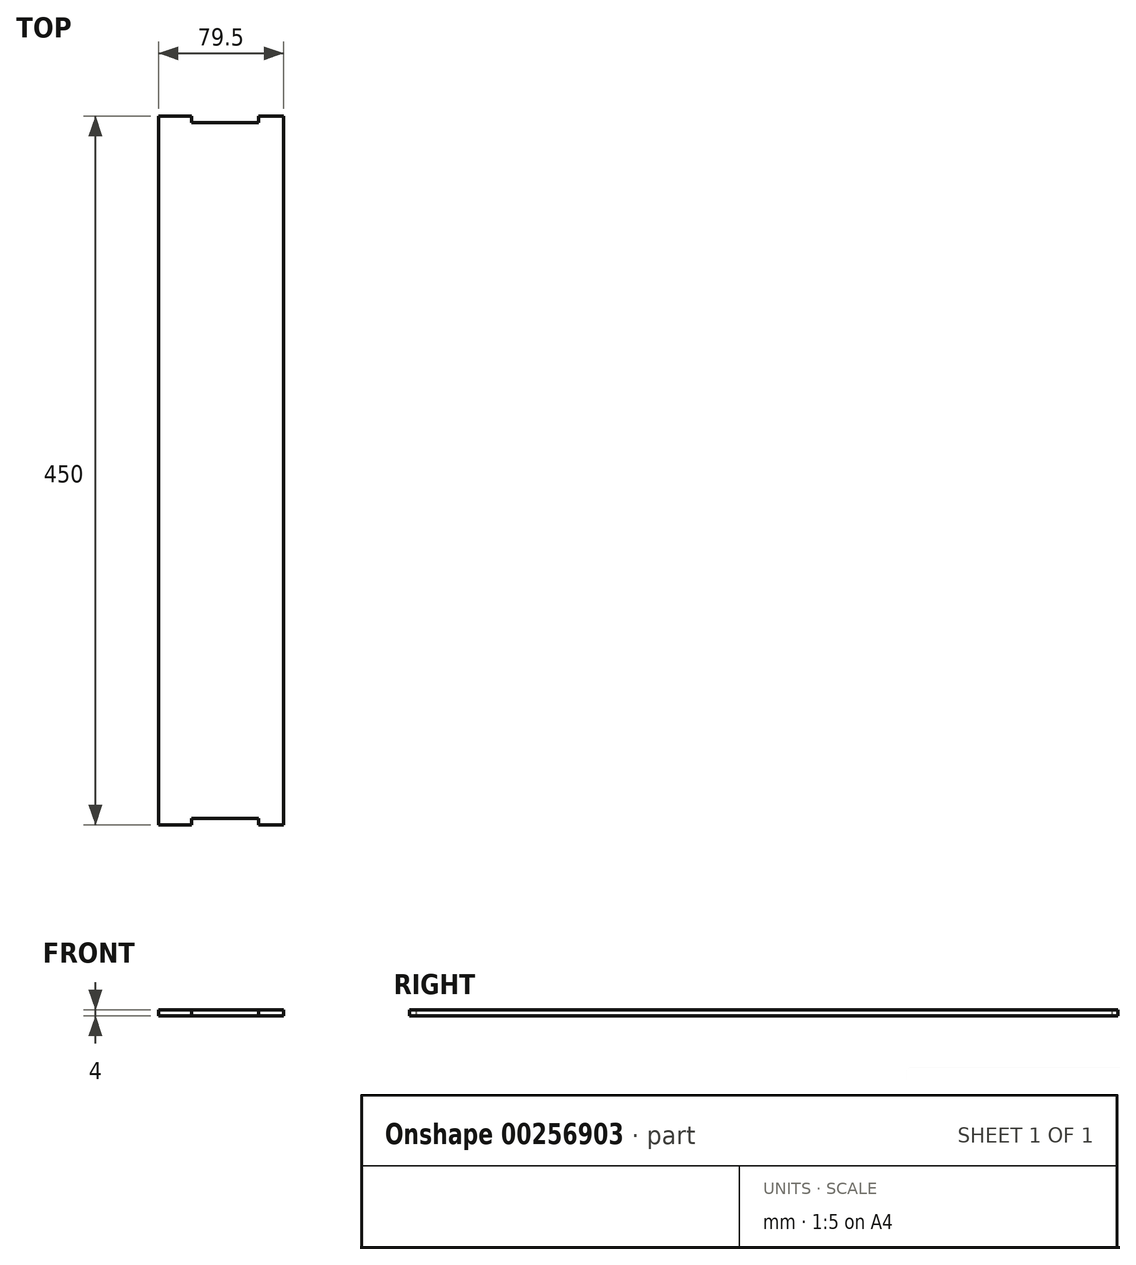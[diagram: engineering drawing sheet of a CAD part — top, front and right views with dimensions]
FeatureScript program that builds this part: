
annotation { "Feature Type Name" : "Feature", "Feature Type Description" : "" }
export const myFeature = defineFeature(function(context is Context, id is Id, definition is map)
    precondition{}
    {
        {
            var Q0;
            Q0=qCreatedBy(makeId("Top.planeOp"),FACE);
            var sketch = newSketch(context, id + "F0", { "sketchPlane" : qUnion([Q0])});
            skLineSegment(sketch, "E0.top", {"start": v(-5.5, 450) * mm, "end": v(-21.25, 450) * mm});
            skLineSegment(sketch, "E0.right", {"start": v(-85, 0) * mm, "end": v(-85, 450) * mm});
            skLineSegment(sketch, "E1", {"start": v(-63.75, 0) * mm, "end": v(-85, 0) * mm});
            skLineSegment(sketch, "E2", {"start": v(-63.75, 0) * mm, "end": v(-63.75, 4) * mm});
            skLineSegment(sketch, "E3", {"start": v(-63.75, 4) * mm, "end": v(-21.25, 4) * mm});
            skLineSegment(sketch, "E4", {"start": v(-21.25, 4) * mm, "end": v(-21.25, 0) * mm});
            skLineSegment(sketch, "E5", {"start": v(-63.75, 450) * mm, "end": v(-85, 450) * mm});
            skLineSegment(sketch, "E6", {"start": v(-63.75, 450) * mm, "end": v(-63.75, 446) * mm});
            skLineSegment(sketch, "E7", {"start": v(-63.75, 446) * mm, "end": v(-21.25, 446) * mm});
            skLineSegment(sketch, "E8", {"start": v(-21.25, 446) * mm, "end": v(-21.25, 450) * mm});
            skLineSegment(sketch, "E9", {"start": v(-5.5, 0) * mm, "end": v(-21.25, 0) * mm});
            skLineSegment(sketch, "E10", {"start": v(-5.5, 0) * mm, "end": v(-5.5, 450) * mm});
            skSolve(sketch);
        }
        {
            var Q0;
            Q0=makeQuery(id+"F0.imprint","IMPRINT",FACE,{"disambiguationData":[TD([[makeQuery(id+"F0.imprint","IMPRINT",EDGE,{"derivedFrom":sQuery(id+"F0.wireOp",EDGE,"E0.top")}),1.0]])]});
            extrude(context, id + "F1", {"entities" : qUnion([Q0]), "depth" : 4 * mm});
        }
    });
